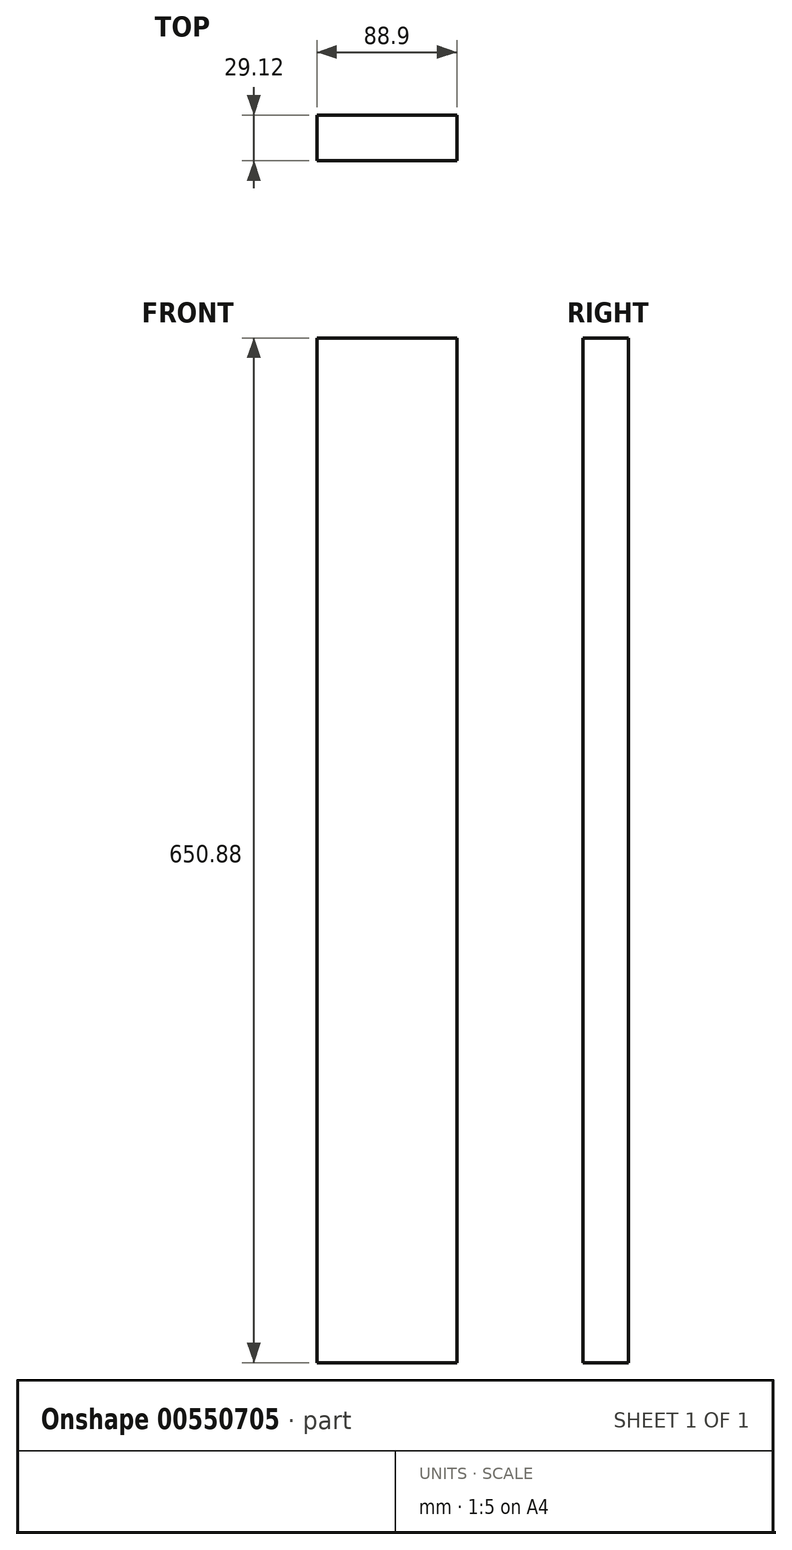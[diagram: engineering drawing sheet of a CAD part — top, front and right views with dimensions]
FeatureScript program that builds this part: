
annotation { "Feature Type Name" : "Feature", "Feature Type Description" : "" }
export const myFeature = defineFeature(function(context is Context, id is Id, definition is map)
    precondition{}
    {
        {
            var Q0;
            Q0=qCreatedBy(makeId("Front.planeOp"),FACE);
            var sketch = newSketch(context, id + "F0", { "sketchPlane" : qUnion([Q0])});
            skLineSegment(sketch, "E0.bottom", {"start": v(-87.28, 446.9) * mm, "end": v(1.62, 446.9) * mm});
            skLineSegment(sketch, "E0.top", {"start": v(-87.28, -203.97) * mm, "end": v(1.62, -203.97) * mm});
            skLineSegment(sketch, "E0.left", {"start": v(-87.28, 446.9) * mm, "end": v(-87.28, -203.97) * mm});
            skLineSegment(sketch, "E0.right", {"start": v(1.62, 446.9) * mm, "end": v(1.62, -203.97) * mm});
            skLineSegment(sketch, "E1", {"start": v(-87.28, 307.2) * mm, "end": v(0, 307.2) * mm});
            skLineSegment(sketch, "E2", {"start": v(-87.28, -197.62) * mm, "end": v(0, -197.62) * mm});
            skSolve(sketch);
        }
        {
            var Q0;
            Q0=makeQuery(id+"F0.imprint","IMPRINT",FACE,{"disambiguationData":[TD([[makeQuery(id+"F0.imprint","IMPRINT",EDGE,{"derivedFrom":sQuery(id+"F0.wireOp",EDGE,"E0.bottom")}),-1.0]])]});
            extrude(context, id + "F1", {"entities" : qUnion([Q0]), "depth" : 29.12 * mm, "offsetDistance" : 25.4 * mm});
        }
    });
